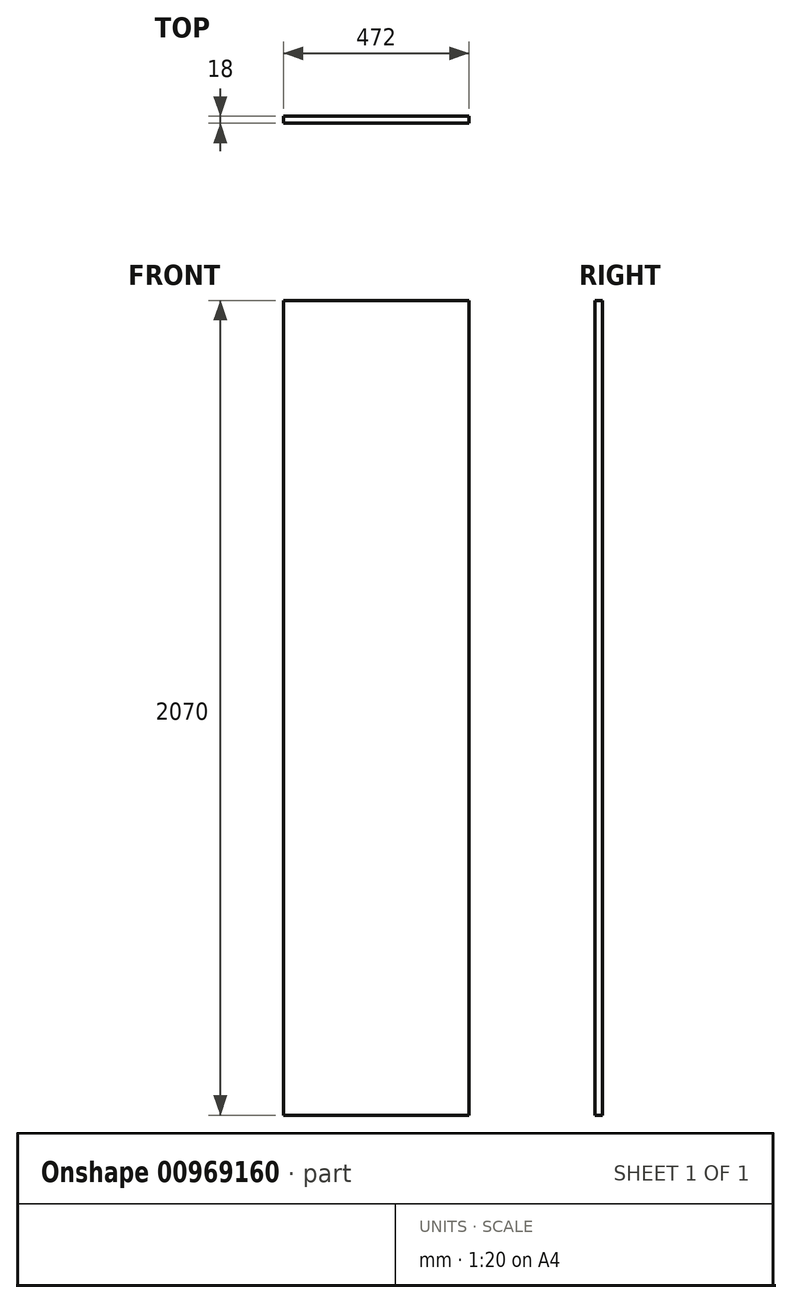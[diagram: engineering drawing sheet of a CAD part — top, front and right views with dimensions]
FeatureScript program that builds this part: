
annotation { "Feature Type Name" : "Feature", "Feature Type Description" : "" }
export const myFeature = defineFeature(function(context is Context, id is Id, definition is map)
    precondition{}
    {
        {
            var Q0;
            Q0=qCreatedBy(makeId("Front.planeOp"),FACE);
            var sketch = newSketch(context, id + "F0", { "sketchPlane" : qUnion([Q0])});
            skLineSegment(sketch, "E0.bottom", {"start": v(0, 0) * mm, "end": v(472, 0) * mm});
            skLineSegment(sketch, "E0.top", {"start": v(0, 2070) * mm, "end": v(472, 2070) * mm});
            skLineSegment(sketch, "E0.left", {"start": v(0, 0) * mm, "end": v(0, 2070) * mm});
            skLineSegment(sketch, "E0.right", {"start": v(472, 0) * mm, "end": v(472, 2070) * mm});
            skSolve(sketch);
        }
        {
            var Q0;
            Q0 = qSketchRegion(id + "F0", true);
            extrude(context, id + "F1", {"entities" : qUnion([Q0]), "depth" : 18 * mm, "offsetDistance" : 25 * mm});
        }
    });
